# Revit family: C_FP20_1_100_2DO_CAD_MULT_Prod
name_source: partatom
category: Detail Items
revit_build: Autodesk Revit 2015 (Build: 20140606_1530(x64)
units: mm (PartAtom-declared; Revit-internal decimal feet)

## types (2) — shared parameters
Density = 12.50 kg
Description = Straps
EPD = https://www.strongtie.eu
ETA / DoP = https://www.strongtie.eu
Manufacturer = Simpson Strong-Tie
Model = FP20/1/100
Model Disclaimer = Contact Simpson Strong-Tie Company  for more information
Model ID = 0059631913434529588481440357020933369964
Name = FP20/1/100
ObjectType = FP20/1/100
Product Material = Galvanised
Product Type = Straps
Reference = FP20/1/100
Technical datasheet = https://www.strongtie.eu
URL = www.strongtie.eu
UniClass Number = Pr_20_29_31_13
UniClass Title = Carbon steel punched metal plate fasteners

## per-type parameters (varying)
| type | _visiblefront | _visibleleft |
| SST_FP20/1/100_Front | Yes | No |
| SST_FP20/1/100_Left | No | Yes |

## geometry (parser evidence)
native form markers: Sweep x5
no freeform markers — native parametric forms only
